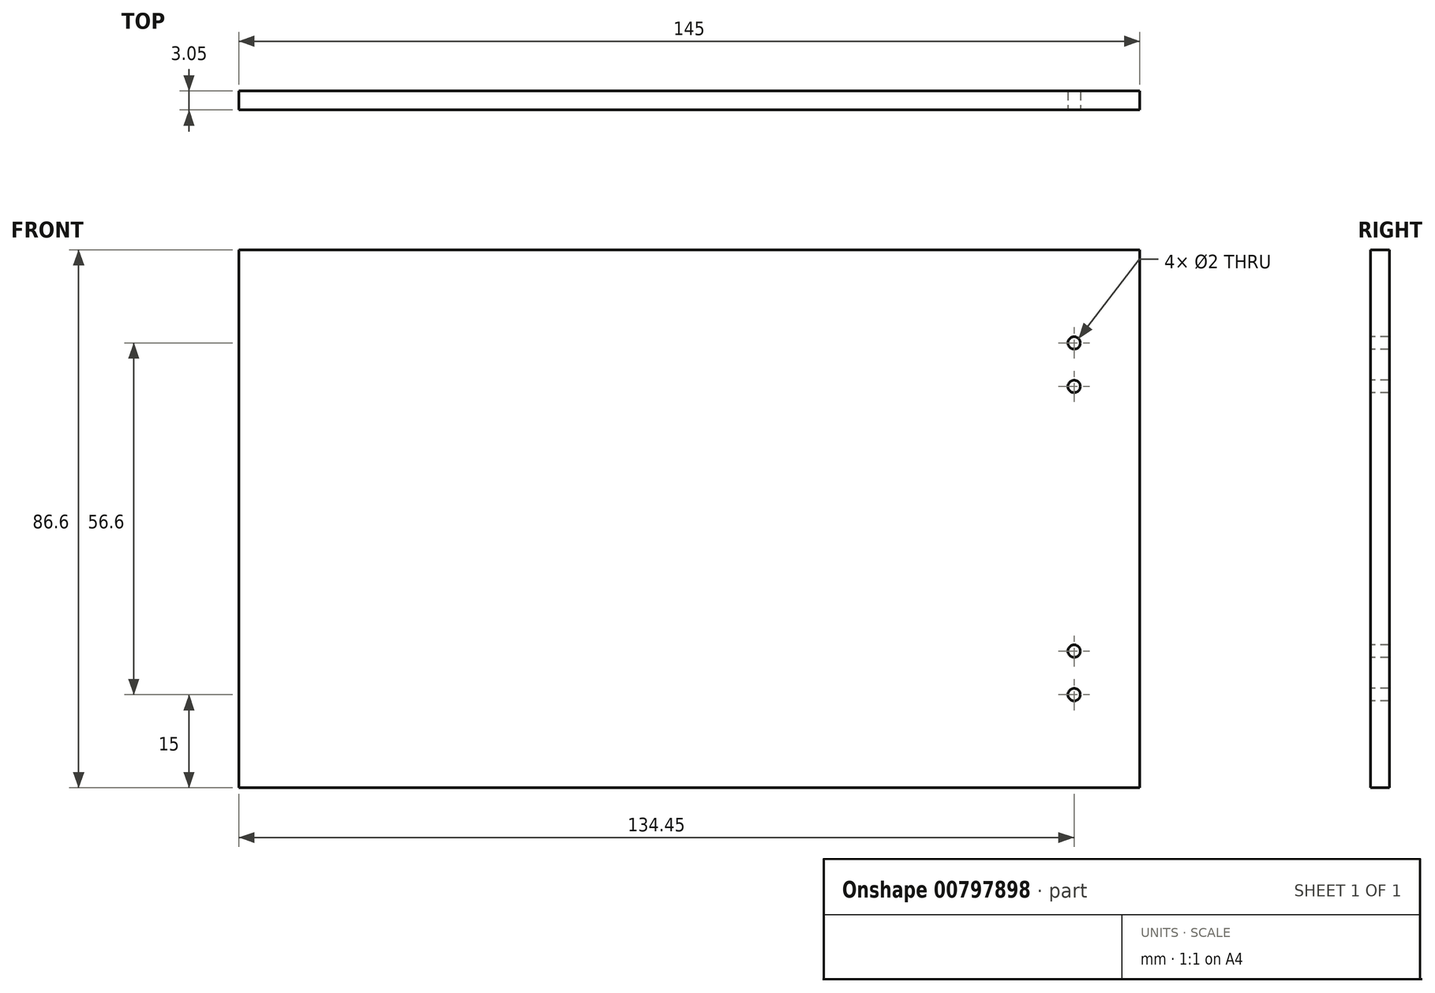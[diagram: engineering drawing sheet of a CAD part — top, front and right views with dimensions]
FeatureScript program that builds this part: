
annotation { "Feature Type Name" : "Feature", "Feature Type Description" : "" }
export const myFeature = defineFeature(function(context is Context, id is Id, definition is map)
    precondition{}
    {
        {
            var Q0;
            Q0=qCreatedBy(makeId("Front.planeOp"),FACE);
            var sketch = newSketch(context, id + "F0", { "sketchPlane" : qUnion([Q0])});
            skLineSegment(sketch, "E0.bottom", {"start": v(72.5, 43.3) * mm, "end": v(-72.5, 43.3) * mm});
            skLineSegment(sketch, "E0.top", {"start": v(72.5, -43.3) * mm, "end": v(-72.5, -43.3) * mm});
            skLineSegment(sketch, "E0.left", {"start": v(72.5, 43.3) * mm, "end": v(72.5, -43.3) * mm});
            skLineSegment(sketch, "E0.right", {"start": v(-72.5, 43.3) * mm, "end": v(-72.5, -43.3) * mm});
            skPoint(sketch, "E0.middle", {"position": v(0, 0) * mm});
            skSolve(sketch);
        }
        {
            var Q0;
            Q0=qSketchRegion(id+"F0",true);
            extrude(context, id + "F1", {"entities" : qUnion([Q0]), "depth" : 3.05 * mm, "offsetDistance" : 25 * mm});
        }
        {
            var Q0;
            Q0=makeQuery(id+"F1.opExtrude","CAP_FACE",FACE,{"disambiguationData":[OSD([sQuery(id+"F0.wireOp",EDGE,"E0.bottom"),sQuery(id+"F0.wireOp",EDGE,"E0.top"),sQuery(id+"F0.wireOp",EDGE,"E0.left"),sQuery(id+"F0.wireOp",EDGE,"E0.right")])],"isStart":false});
            var sketch = newSketch(context, id + "F2", { "sketchPlane" : qUnion([Q0])});
            skCircle(sketch, "E1", {"center": v(61.95, 28.3) * mm, "radius": 1 * mm});
            skLineSegment(sketch, "E2", {"start": v(61.95, 28.3) * mm, "end": v(61.95, 21.3) * mm, "construction": true});
            skCircle(sketch, "E3", {"center": v(61.95, 21.3) * mm, "radius": 1 * mm});
            skLineSegment(sketch, "E4", {"start": v(61.95, -21.3) * mm, "end": v(61.95, -28.3) * mm, "construction": true});
            skCircle(sketch, "E5", {"center": v(61.95, -21.3) * mm, "radius": 1 * mm});
            skCircle(sketch, "E6", {"center": v(61.95, -28.3) * mm, "radius": 1 * mm});
            skSolve(sketch);
        }
        {
            var Q0;
            Q0=qSketchRegion(id+"F2",true);
            extrude(context, id + "F3", {"entities" : qUnion([Q0]), "operationType" : NewBodyOperationType.REMOVE, "oppositeDirection" : true, "depth" : 25 * mm, "offsetDistance" : 25 * mm});
        }
    });
